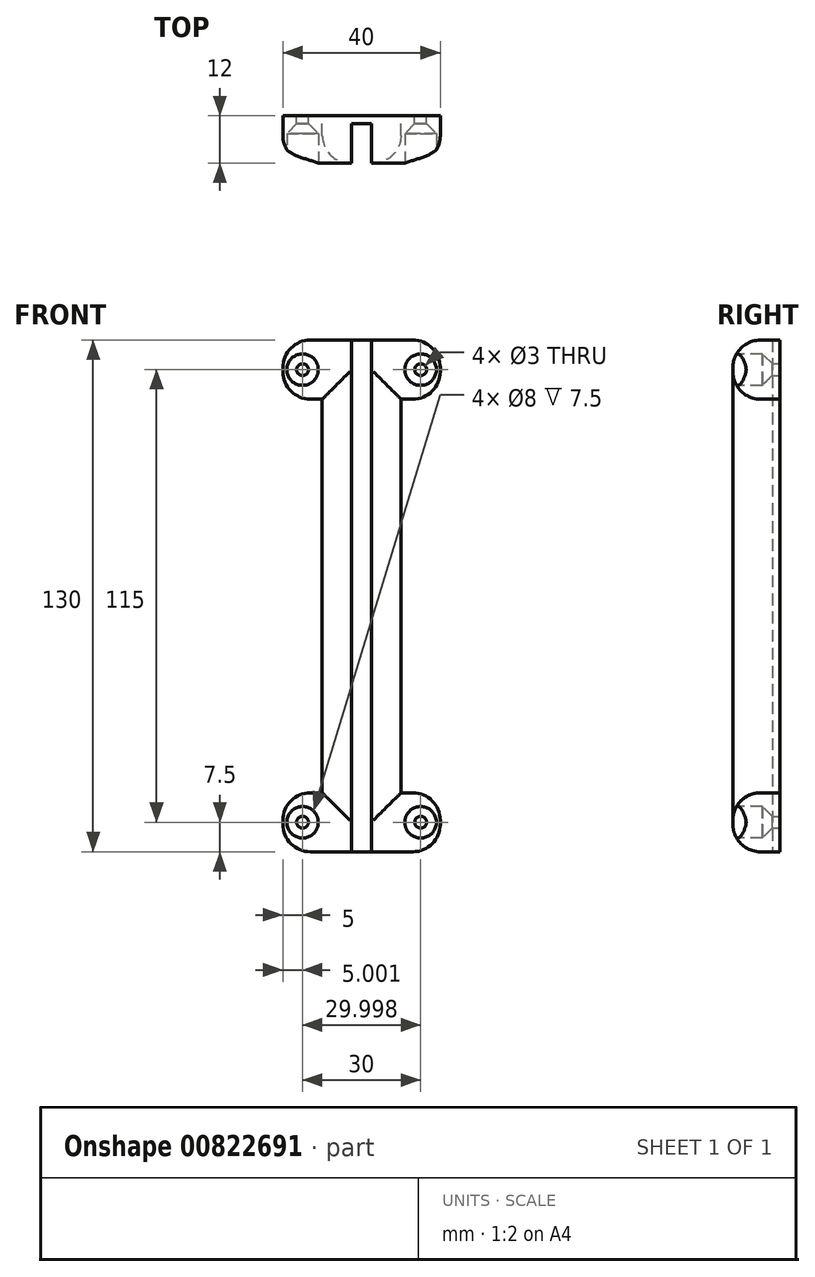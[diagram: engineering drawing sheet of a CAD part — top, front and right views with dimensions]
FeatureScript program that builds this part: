
annotation { "Feature Type Name" : "Feature", "Feature Type Description" : "" }
export const myFeature = defineFeature(function(context is Context, id is Id, definition is map)
    precondition{}
    {
        {
            var Q0;
            Q0=qCreatedBy(makeId("Front.planeOp"),FACE);
            var sketch = newSketch(context, id + "F0", { "sketchPlane" : qUnion([Q0])});
            skLineSegment(sketch, "E0", {"start": v(0, 65) * mm, "end": v(-20, 65) * mm});
            skLineSegment(sketch, "E1", {"start": v(-20, 65) * mm, "end": v(-20, 50) * mm});
            skLineSegment(sketch, "E2", {"start": v(-20, 50) * mm, "end": v(-10, 50) * mm});
            skLineSegment(sketch, "E3", {"start": v(-10, 50) * mm, "end": v(-10, 0) * mm});
            skCircle(sketch, "E4", {"center": v(-15, 57.5) * mm, "radius": 1.5 * mm});
            skLineSegment(sketch, "E5.MirrorCS", {"start": v(0, 65) * mm, "end": v(20, 65) * mm});
            skLineSegment(sketch, "E6.MirrorCS", {"start": v(20, 65) * mm, "end": v(20, 50) * mm});
            skLineSegment(sketch, "E7.MirrorCS", {"start": v(20, 50) * mm, "end": v(10, 50) * mm});
            skCircle(sketch, "E8.MirrorC", {"center": v(15, 57.5) * mm, "radius": 1.5 * mm});
            skLineSegment(sketch, "E9.MirrorCS", {"start": v(10, 50) * mm, "end": v(10, 0) * mm});
            skLineSegment(sketch, "E10.MirrorCS", {"start": v(-10, -50) * mm, "end": v(-10, 0) * mm});
            skLineSegment(sketch, "E11.MirrorCS", {"start": v(-20, -65) * mm, "end": v(-20, -50) * mm});
            skLineSegment(sketch, "E12.MirrorCS", {"start": v(-20, -50) * mm, "end": v(-10, -50) * mm});
            skLineSegment(sketch, "E13.MirrorCS", {"start": v(0, -65) * mm, "end": v(-20, -65) * mm});
            skCircle(sketch, "E14.MirrorC", {"center": v(15, -57.5) * mm, "radius": 1.5 * mm});
            skLineSegment(sketch, "E15.MirrorCS", {"start": v(0, -65) * mm, "end": v(20, -65) * mm});
            skLineSegment(sketch, "E16.MirrorCS", {"start": v(20, -50) * mm, "end": v(10, -50) * mm});
            skCircle(sketch, "E17.MirrorC", {"center": v(-15, -57.5) * mm, "radius": 1.5 * mm});
            skLineSegment(sketch, "E18.MirrorCS", {"start": v(10, -50) * mm, "end": v(10, 0) * mm});
            skLineSegment(sketch, "E19.MirrorCS", {"start": v(20, -65) * mm, "end": v(20, -50) * mm});
            skSolve(sketch);
        }
        {
            var Q0;
            Q0 = qSketchRegion(id + "F0", true);
            extrude(context, id + "F1", {"entities" : qUnion([Q0]), "depth" : 12 * mm, "offsetDistance" : 25 * mm});
        }
        {
            var Q0;
            Q0=makeQuery(id+"F1.opExtrude","CAP_FACE",FACE,{"disambiguationData":[OSD([sQuery(id+"F0.wireOp",EDGE,"E0"),sQuery(id+"F0.wireOp",EDGE,"E1"),sQuery(id+"F0.wireOp",EDGE,"E2"),sQuery(id+"F0.wireOp",EDGE,"E3"),sQuery(id+"F0.wireOp",EDGE,"E4"),sQuery(id+"F0.wireOp",EDGE,"E5.MirrorCS"),sQuery(id+"F0.wireOp",EDGE,"E6.MirrorCS"),sQuery(id+"F0.wireOp",EDGE,"E7.MirrorCS"),sQuery(id+"F0.wireOp",EDGE,"E8.MirrorC"),sQuery(id+"F0.wireOp",EDGE,"E9.MirrorCS"),sQuery(id+"F0.wireOp",EDGE,"E10.MirrorCS"),sQuery(id+"F0.wireOp",EDGE,"E11.MirrorCS"),sQuery(id+"F0.wireOp",EDGE,"E12.MirrorCS"),sQuery(id+"F0.wireOp",EDGE,"E13.MirrorCS"),sQuery(id+"F0.wireOp",EDGE,"E14.MirrorC"),sQuery(id+"F0.wireOp",EDGE,"E15.MirrorCS"),sQuery(id+"F0.wireOp",EDGE,"E16.MirrorCS"),sQuery(id+"F0.wireOp",EDGE,"E17.MirrorC"),sQuery(id+"F0.wireOp",EDGE,"E18.MirrorCS"),sQuery(id+"F0.wireOp",EDGE,"E19.MirrorCS")])],"isStart":false});
            var sketch = newSketch(context, id + "F2", { "sketchPlane" : qUnion([Q0])});
            skLineSegment(sketch, "E20.0", {"start": v(-2.5, 65) * mm, "end": v(-2.5, -65) * mm});
            skLineSegment(sketch, "E21.0", {"start": v(2.5, 65) * mm, "end": v(2.5, -65) * mm});
            skLineSegment(sketch, "E22", {"start": v(-2.5, 65) * mm, "end": v(2.5, 65) * mm});
            skLineSegment(sketch, "E23", {"start": v(-2.5, -65) * mm, "end": v(2.5, -65) * mm});
            skSolve(sketch);
        }
        {
            var Q0;
            Q0 = qSketchRegion(id + "F2", true);
            extrude(context, id + "F3", {"entities" : qUnion([Q0]), "operationType" : NewBodyOperationType.REMOVE, "oppositeDirection" : true, "depth" : 10 * mm, "offsetDistance" : 25 * mm});
        }
        {
            var Q0;
            {var subQ0=sQuery(id+"F0.wireOp",EDGE,"E15.MirrorCS");var subQ1=sQuery(id+"F0.wireOp",EDGE,"E13.MirrorCS");var subQ2=sQuery(id+"F0.wireOp",EDGE,"E11.MirrorCS");Q0=makeQuery(id+"F3.boolean.opBoolean","SPLIT",EDGE,{"disambiguationData":[TD([makeQuery(id+"F1.opExtrude","SWEPT_FACE",FACE,{"disambiguationData":[OSD([subQ2])]})])],"derivedFrom":makeQuery(id+"F1.opExtrude","CAP_EDGE",EDGE,{"disambiguationData":[OSD([subQ1,subQ0])],"isStart":false})});}
            var Q1;
            Q1=makeQuery(id+"F1.opExtrude","CAP_EDGE",EDGE,{"disambiguationData":[OSD([sQuery(id+"F0.wireOp",EDGE,"E11.MirrorCS")])],"isStart":false});
            var Q2;
            Q2=makeQuery(id+"F1.opExtrude","CAP_EDGE",EDGE,{"disambiguationData":[OSD([sQuery(id+"F0.wireOp",EDGE,"E12.MirrorCS")])],"isStart":false});
            var Q3;
            Q3=makeQuery(id+"F1.opExtrude","CAP_EDGE",EDGE,{"disambiguationData":[OSD([sQuery(id+"F0.wireOp",EDGE,"E3"),sQuery(id+"F0.wireOp",EDGE,"E10.MirrorCS")])],"isStart":false});
            var Q4;
            Q4=makeQuery(id+"F1.opExtrude","CAP_EDGE",EDGE,{"disambiguationData":[OSD([sQuery(id+"F0.wireOp",EDGE,"E2")])],"isStart":false});
            var Q5;
            Q5=makeQuery(id+"F1.opExtrude","CAP_EDGE",EDGE,{"disambiguationData":[OSD([sQuery(id+"F0.wireOp",EDGE,"E1")])],"isStart":false});
            var Q6;
            {var subQ0=sQuery(id+"F0.wireOp",EDGE,"E5.MirrorCS");var subQ1=sQuery(id+"F0.wireOp",EDGE,"E1");var subQ2=sQuery(id+"F0.wireOp",EDGE,"E0");Q6=makeQuery(id+"F3.boolean.opBoolean","SPLIT",EDGE,{"disambiguationData":[TD([makeQuery(id+"F1.opExtrude","SWEPT_FACE",FACE,{"disambiguationData":[OSD([subQ1])]})])],"derivedFrom":makeQuery(id+"F1.opExtrude","CAP_EDGE",EDGE,{"disambiguationData":[OSD([subQ2,subQ0])],"isStart":false})});}
            var Q7;
            {var subQ0=sQuery(id+"F0.wireOp",EDGE,"E6.MirrorCS");var subQ1=sQuery(id+"F0.wireOp",EDGE,"E5.MirrorCS");var subQ2=sQuery(id+"F0.wireOp",EDGE,"E0");Q7=makeQuery(id+"F3.boolean.opBoolean","SPLIT",EDGE,{"disambiguationData":[TD([makeQuery(id+"F1.opExtrude","SWEPT_FACE",FACE,{"disambiguationData":[OSD([subQ0])]})])],"derivedFrom":makeQuery(id+"F1.opExtrude","CAP_EDGE",EDGE,{"disambiguationData":[OSD([subQ2,subQ1])],"isStart":false})});}
            var Q8;
            Q8=makeQuery(id+"F1.opExtrude","CAP_EDGE",EDGE,{"disambiguationData":[OSD([sQuery(id+"F0.wireOp",EDGE,"E6.MirrorCS")])],"isStart":false});
            var Q9;
            Q9=makeQuery(id+"F1.opExtrude","CAP_EDGE",EDGE,{"disambiguationData":[OSD([sQuery(id+"F0.wireOp",EDGE,"E7.MirrorCS")])],"isStart":false});
            var Q10;
            Q10=makeQuery(id+"F1.opExtrude","CAP_EDGE",EDGE,{"disambiguationData":[OSD([sQuery(id+"F0.wireOp",EDGE,"E9.MirrorCS"),sQuery(id+"F0.wireOp",EDGE,"E18.MirrorCS")])],"isStart":false});
            var Q11;
            Q11=makeQuery(id+"F1.opExtrude","CAP_EDGE",EDGE,{"disambiguationData":[OSD([sQuery(id+"F0.wireOp",EDGE,"E16.MirrorCS")])],"isStart":false});
            var Q12;
            Q12=makeQuery(id+"F1.opExtrude","CAP_EDGE",EDGE,{"disambiguationData":[OSD([sQuery(id+"F0.wireOp",EDGE,"E19.MirrorCS")])],"isStart":false});
            var Q13;
            {var subQ0=sQuery(id+"F0.wireOp",EDGE,"E19.MirrorCS");var subQ1=sQuery(id+"F0.wireOp",EDGE,"E15.MirrorCS");var subQ2=sQuery(id+"F0.wireOp",EDGE,"E13.MirrorCS");Q13=makeQuery(id+"F3.boolean.opBoolean","SPLIT",EDGE,{"disambiguationData":[TD([makeQuery(id+"F1.opExtrude","SWEPT_FACE",FACE,{"disambiguationData":[OSD([subQ0])]})])],"derivedFrom":makeQuery(id+"F1.opExtrude","CAP_EDGE",EDGE,{"disambiguationData":[OSD([subQ2,subQ1])],"isStart":false})});}
            fillet(context, id + "F4", {"entities" : qUnion([Q0, Q1, Q2, Q3, Q4, Q5, Q6, Q7, Q8, Q9, Q10, Q11, Q12, Q13]), "radius" : 7 * mm, "tangentPropagation" : true, "allowEdgeOverflow" : false});
        }
        {
            var Q0;
            Q0=makeQuery(id+"F1.opExtrude","SWEPT_EDGE",EDGE,{"disambiguationData":[OSD([sQuery(id+"F0.wireOp",EDGE,"E16.MirrorCS"),sQuery(id+"F0.wireOp",EDGE,"E19.MirrorCS")])]});
            var Q1;
            Q1=makeQuery(id+"F1.opExtrude","SWEPT_EDGE",EDGE,{"disambiguationData":[OSD([sQuery(id+"F0.wireOp",EDGE,"E15.MirrorCS"),sQuery(id+"F0.wireOp",EDGE,"E19.MirrorCS")])]});
            var Q2;
            Q2=makeQuery(id+"F1.opExtrude","SWEPT_EDGE",EDGE,{"disambiguationData":[OSD([sQuery(id+"F0.wireOp",EDGE,"E6.MirrorCS"),sQuery(id+"F0.wireOp",EDGE,"E7.MirrorCS")])]});
            var Q3;
            Q3=makeQuery(id+"F1.opExtrude","SWEPT_EDGE",EDGE,{"disambiguationData":[OSD([sQuery(id+"F0.wireOp",EDGE,"E5.MirrorCS"),sQuery(id+"F0.wireOp",EDGE,"E6.MirrorCS")])]});
            var Q4;
            Q4=makeQuery(id+"F1.opExtrude","SWEPT_EDGE",EDGE,{"disambiguationData":[OSD([sQuery(id+"F0.wireOp",EDGE,"E0"),sQuery(id+"F0.wireOp",EDGE,"E1")])]});
            var Q5;
            Q5=makeQuery(id+"F1.opExtrude","SWEPT_EDGE",EDGE,{"disambiguationData":[OSD([sQuery(id+"F0.wireOp",EDGE,"E1"),sQuery(id+"F0.wireOp",EDGE,"E2")])]});
            var Q6;
            Q6=makeQuery(id+"F1.opExtrude","SWEPT_EDGE",EDGE,{"disambiguationData":[OSD([sQuery(id+"F0.wireOp",EDGE,"E11.MirrorCS"),sQuery(id+"F0.wireOp",EDGE,"E13.MirrorCS")])]});
            var Q7;
            Q7=makeQuery(id+"F1.opExtrude","SWEPT_EDGE",EDGE,{"disambiguationData":[OSD([sQuery(id+"F0.wireOp",EDGE,"E11.MirrorCS"),sQuery(id+"F0.wireOp",EDGE,"E12.MirrorCS")])]});
            fillet(context, id + "F5", {"entities" : qUnion([Q0, Q1, Q2, Q3, Q4, Q5, Q6, Q7]), "radius" : 7 * mm, "tangentPropagation" : true, "allowEdgeOverflow" : false});
        }
        {
            var Q0;
            {var subQ0=sQuery(id+"F0.wireOp",EDGE,"E10.MirrorCS");var subQ1=sQuery(id+"F0.wireOp",EDGE,"E3");var subQ2=sQuery(id+"F0.wireOp",EDGE,"E17.MirrorC");var subQ3=sQuery(id+"F0.wireOp",EDGE,"E2");var subQ4=sQuery(id+"F0.wireOp",EDGE,"E1");var subQ5=sQuery(id+"F0.wireOp",EDGE,"E5.MirrorCS");var subQ6=sQuery(id+"F0.wireOp",EDGE,"E0");var subQ7=sQuery(id+"F0.wireOp",EDGE,"E15.MirrorCS");var subQ8=sQuery(id+"F0.wireOp",EDGE,"E13.MirrorCS");var subQ9=sQuery(id+"F0.wireOp",EDGE,"E4");var subQ10=sQuery(id+"F0.wireOp",EDGE,"E11.MirrorCS");var subQ11=sQuery(id+"F0.wireOp",EDGE,"E12.MirrorCS");Q0=makeQuery(id+"F3.boolean.opBoolean","SPLIT",FACE,{"disambiguationData":[TD([makeQuery(id+"F1.opExtrude","SWEPT_FACE",FACE,{"disambiguationData":[OSD([subQ4])]})])],"derivedFrom":makeQuery(id+"F1.opExtrude","CAP_FACE",FACE,{"disambiguationData":[OSD([subQ6,subQ4,subQ3,subQ1,subQ9,subQ5,sQuery(id+"F0.wireOp",EDGE,"E6.MirrorCS"),sQuery(id+"F0.wireOp",EDGE,"E7.MirrorCS"),sQuery(id+"F0.wireOp",EDGE,"E8.MirrorC"),sQuery(id+"F0.wireOp",EDGE,"E9.MirrorCS"),subQ0,subQ10,subQ11,subQ8,sQuery(id+"F0.wireOp",EDGE,"E14.MirrorC"),subQ7,sQuery(id+"F0.wireOp",EDGE,"E16.MirrorCS"),subQ2,sQuery(id+"F0.wireOp",EDGE,"E18.MirrorCS"),sQuery(id+"F0.wireOp",EDGE,"E19.MirrorCS")])],"isStart":false})});}
            var sketch = newSketch(context, id + "F6", { "sketchPlane" : qUnion([Q0])});
            skCircle(sketch, "E24", {"center": v(-15, 57.5) * mm, "radius": 4 * mm});
            skPoint(sketch, "E24.centerSnap0", {"position": v(-13, 57.5) * mm});
            skCircle(sketch, "E25.MirrorC", {"center": v(15, 57.5) * mm, "radius": 4 * mm});
            skCircle(sketch, "E26.MirrorC", {"center": v(-15, -57.5) * mm, "radius": 4 * mm});
            skCircle(sketch, "E27.MirrorC", {"center": v(15, -57.5) * mm, "radius": 4 * mm});
            skSolve(sketch);
        }
        {
            var Q0;
            Q0 = qSketchRegion(id + "F6", true);
            extrude(context, id + "F7", {"entities" : qUnion([Q0]), "operationType" : NewBodyOperationType.REMOVE, "oppositeDirection" : true, "depth" : 7 * mm, "offsetDistance" : 25 * mm});
        }
        {
            var Q0;
            Q0=makeQuery(id+"F7.boolean.opBoolean","INTERSECT",EDGE,{"derivedFrom":[makeQuery(id+"F1.opExtrude","SWEPT_FACE",FACE,{"disambiguationData":[OSD([sQuery(id+"F0.wireOp",EDGE,"E4")])]}),makeQuery(id+"F7.opExtrude","CAP_FACE",FACE,{"disambiguationData":[OSD([sQuery(id+"F6.wireOp",EDGE,"E24")])],"isStart":false})]});
            var Q1;
            Q1=makeQuery(id+"F7.boolean.opBoolean","INTERSECT",EDGE,{"derivedFrom":[makeQuery(id+"F1.opExtrude","SWEPT_FACE",FACE,{"disambiguationData":[OSD([sQuery(id+"F0.wireOp",EDGE,"E8.MirrorC")])]}),makeQuery(id+"F7.opExtrude","CAP_FACE",FACE,{"disambiguationData":[OSD([sQuery(id+"F6.wireOp",EDGE,"E25.MirrorC")])],"isStart":false})]});
            var Q2;
            Q2=makeQuery(id+"F7.boolean.opBoolean","INTERSECT",EDGE,{"derivedFrom":[makeQuery(id+"F1.opExtrude","SWEPT_FACE",FACE,{"disambiguationData":[OSD([sQuery(id+"F0.wireOp",EDGE,"E17.MirrorC")])]}),makeQuery(id+"F7.opExtrude","CAP_FACE",FACE,{"disambiguationData":[OSD([sQuery(id+"F6.wireOp",EDGE,"E26.MirrorC")])],"isStart":false})]});
            var Q3;
            Q3=makeQuery(id+"F7.boolean.opBoolean","INTERSECT",EDGE,{"derivedFrom":[makeQuery(id+"F1.opExtrude","SWEPT_FACE",FACE,{"disambiguationData":[OSD([sQuery(id+"F0.wireOp",EDGE,"E14.MirrorC")])]}),makeQuery(id+"F7.opExtrude","CAP_FACE",FACE,{"disambiguationData":[OSD([sQuery(id+"F6.wireOp",EDGE,"E27.MirrorC")])],"isStart":false})]});
            chamfer(context, id + "F8", {"entities" : qUnion([Q0, Q1, Q2, Q3]), "width" : 3 * mm, "tangentPropagation" : true});
        }
    });
